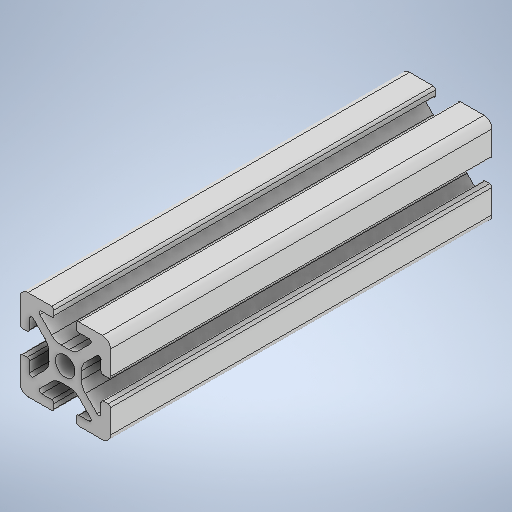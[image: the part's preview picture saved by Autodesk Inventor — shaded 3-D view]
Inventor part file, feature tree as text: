
AUTODESK INVENTOR PART (.ipt)
format: ipt  version: 2025.1 (Build 291241000, 241)  size: 329,728 bytes
history: native  units: in
note: dims shown in document units (in); Inventor stores cm internally (conversion verified against a paired STEP export)
features: direct_edit x1, mirror x1, move_body x1
ambient origin geometry x8: Origin, YZ Plane, XZ Plane, XY Plane, X Axis, Y Axis, Z Axis, Center Point
bodies: Solid1 (feature_tree)
feature tree (3):
  direct_edit  "Direct Edit2"
  mirror  "Mirror2"
  move_body  "Move2"
